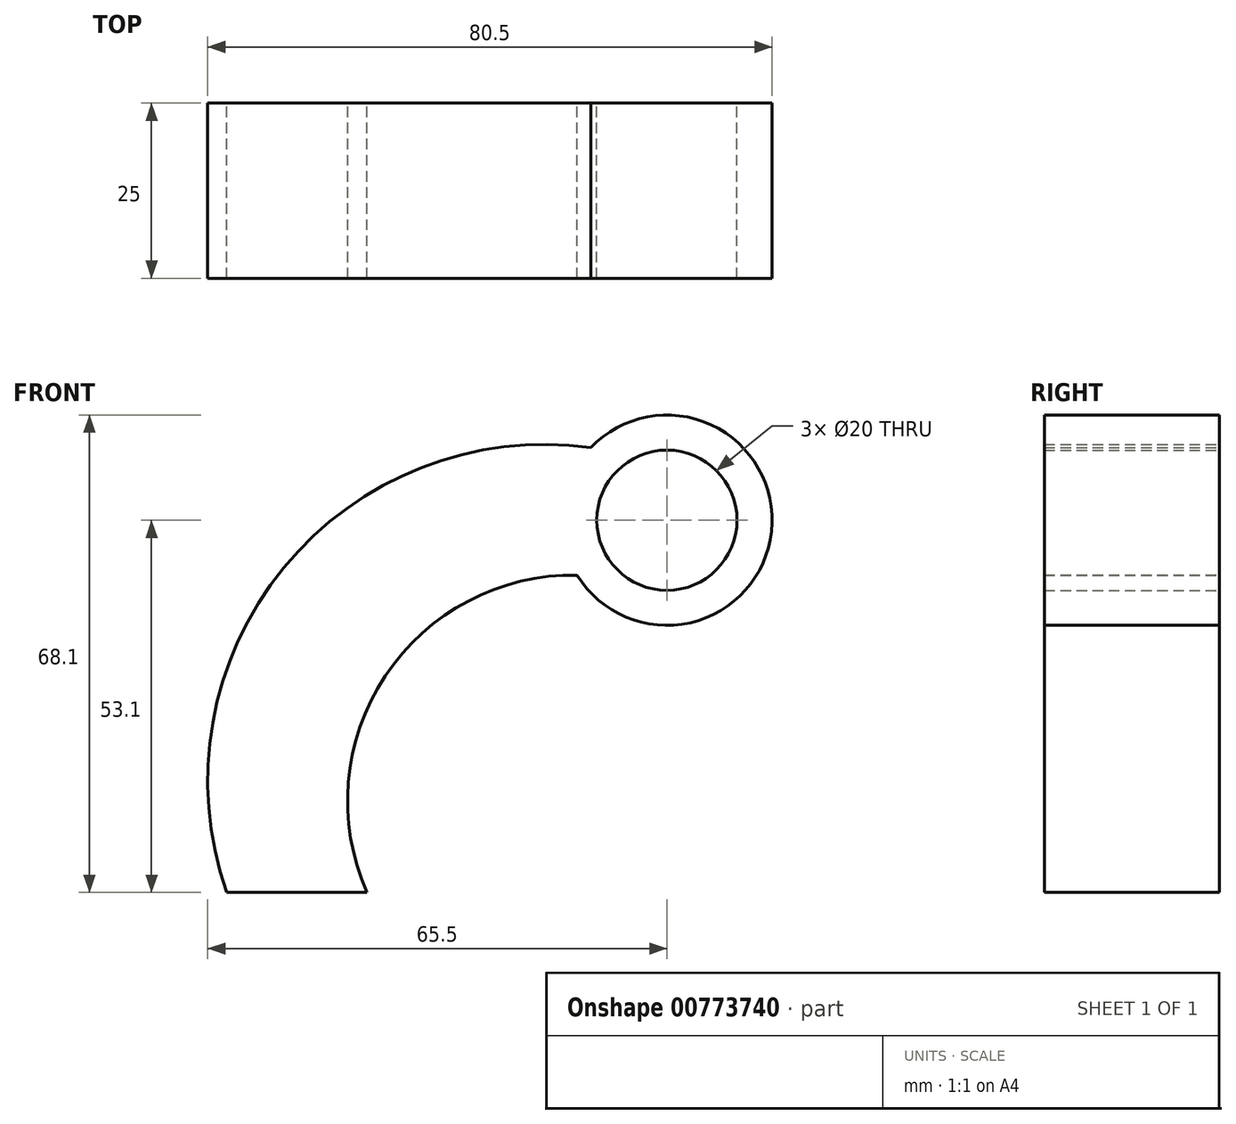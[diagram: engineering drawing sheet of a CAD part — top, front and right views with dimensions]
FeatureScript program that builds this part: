
annotation { "Feature Type Name" : "Feature", "Feature Type Description" : "" }
export const myFeature = defineFeature(function(context is Context, id is Id, definition is map)
    precondition{}
    {
        {
            var Q0;
            Q0=qCreatedBy(makeId("Front.planeOp"),FACE);
            var sketch = newSketch(context, id + "F0", { "sketchPlane" : qUnion([Q0])});
            skCircle(sketch, "E0", {"center": v(0, 0) * mm, "radius": 15 * mm});
            skCircle(sketch, "E1", {"center": v(0, 0) * mm, "radius": 10 * mm});
            skArc(sketch, "E2", {"start": v(-12.8, -7.83) * mm, "mid": v(-40.2, -22.24) * mm, "end": v(-42.78, -53.1) * mm});
            skArc(sketch, "E3", {"start": v(-10.87, 10.34) * mm, "mid": v(-54.66, -6.78) * mm, "end": v(-62.78, -53.1) * mm});
            skLineSegment(sketch, "E4", {"start": v(-62.78, -53.1) * mm, "end": v(-42.78, -53.1) * mm});
            skSolve(sketch);
        }
        {
            var Q0;
            {var subQ0=sQuery(id+"F0.wireOp",EDGE,"E2");Q0=makeQuery(id+"F0.imprint","IMPRINT",FACE,{"disambiguationData":[TD([[makeQuery(id+"F0.imprint","IMPRINT",EDGE,{"derivedFrom":subQ0}),-1.0]])]});}
            var Q1;
            Q1=makeQuery(id+"F0.imprint","IMPRINT",FACE,{"disambiguationData":[TD([[makeQuery(id+"F0.imprint","IMPRINT",EDGE,{"derivedFrom":sQuery(id+"F0.wireOp",EDGE,"E1")}),-1.0]])]});
            extrude(context, id + "F1", {"entities" : qUnion([Q0, Q1]), "depth" : 25 * mm, "offsetDistance" : 25 * mm});
        }
    });
